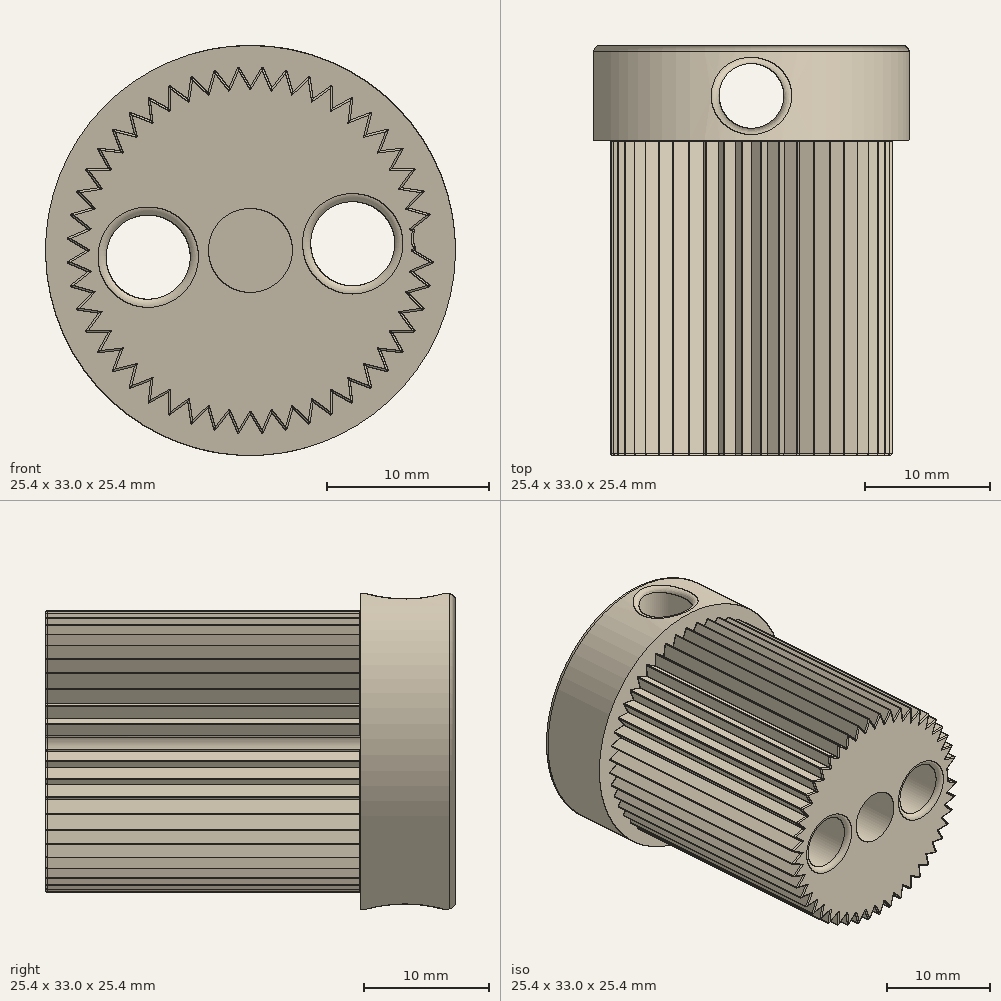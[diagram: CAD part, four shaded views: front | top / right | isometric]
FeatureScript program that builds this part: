
annotation { "Feature Type Name" : "Feature", "Feature Type Description" : "" }
export const myFeature = defineFeature(function(context is Context, id is Id, definition is map)
    precondition{}
    {
        {
            var Q0;
            Q0=qCreatedBy(makeId("Front.planeOp"),FACE);
            var sketch = newSketch(context, id + "F0", { "sketchPlane" : qUnion([Q0])});
            skCircle(sketch, "E0", {"center": v(0, 0) * mm, "radius": 10.16 * mm, "construction": true});
            skCircle(sketch, "E1", {"center": v(0, 0) * mm, "radius": 11.43 * mm, "construction": true});
            skLineSegment(sketch, "E2", {"start": v(0, 0) * mm, "end": v(24.31, 0) * mm, "construction": true});
            skLineSegment(sketch, "E3", {"start": v(0, 0) * mm, "end": v(24.33, -1.6) * mm, "construction": true});
            skLineSegment(sketch, "E4", {"start": v(0, 0) * mm, "end": v(10.07, -1.33) * mm, "construction": true});
            skLineSegment(sketch, "E5", {"start": v(9.53, 0) * mm, "end": v(10.16, 0) * mm});
            skLineSegment(sketch, "E6", {"start": v(10.16, 0) * mm, "end": v(11.4, -0.75) * mm});
            skLineSegment(sketch, "E7", {"start": v(10.07, -1.33) * mm, "end": v(9.44, -1.24) * mm});
            skLineSegment(sketch, "E8", {"start": v(0, 0) * mm, "end": v(9.53, 0) * mm});
            skLineSegment(sketch, "E9", {"start": v(0, 0) * mm, "end": v(9.44, -1.24) * mm});
            skLineSegment(sketch, "E10", {"start": v(11.4, -0.75) * mm, "end": v(10.07, -1.33) * mm});
            skLineSegment(sketch, "E11.trimOffspring", {"start": v(11.33, -1.5) * mm, "end": v(23.43, -3.08) * mm, "construction": true});
            skPoint(sketch, "E12.orphan", {"position": v(10.16, -1.34) * mm});
            skLineSegment(sketch, "E13", {"start": v(17.07, 1.12) * mm, "end": v(-16.43, -1.08) * mm, "construction": true});
            skCircle(sketch, "E14", {"center": v(0, 0) * mm, "radius": 6.35 * mm, "construction": true});
            skCircle(sketch, "E15", {"center": v(-6.34, -0.42) * mm, "radius": 2.6 * mm});
            skCircle(sketch, "E16", {"center": v(6.34, 0.42) * mm, "radius": 2.6 * mm});
            skSolve(sketch);
        }
        {
            var Q0;
            Q0=makeQuery(id+"F0.imprint","IMPRINT",FACE,{"disambiguationData":[TD([[makeQuery(id+"F0.imprint","IMPRINT",EDGE,{"derivedFrom":sQuery(id+"F0.wireOp",EDGE,"E5")}),-1.0]])]});
            var Q1;
            {var subQ0=sQuery(id+"F0.wireOp",EDGE,"E16");var subQ1=sQuery(id+"F0.wireOp",EDGE,"E8");var subQ2=makeQuery(id+"F0.imprint","INTERSECT",VERTEX,{"disambiguationData":[OD(0.0)],"derivedFrom":[subQ1,subQ0]});Q1=makeQuery(id+"F0.imprint","IMPRINT",FACE,{"disambiguationData":[TD([[makeQuery(id+"F0.imprint","IMPRINT",EDGE,{"disambiguationData":[TD([[subQ2,-1.0]])],"derivedFrom":subQ1}),-1.0]])]});}
            var Q2;
            {var subQ0=sQuery(id+"F0.wireOp",EDGE,"E9");var subQ1=sQuery(id+"F0.wireOp",EDGE,"E8");var subQ2=makeQuery(id+"F0.imprint","INTERSECT",VERTEX,{"derivedFrom":[subQ1,subQ0]});Q2=makeQuery(id+"F0.imprint","IMPRINT",FACE,{"disambiguationData":[TD([[makeQuery(id+"F0.imprint","IMPRINT",EDGE,{"disambiguationData":[TD([[subQ2,-1.0]])],"derivedFrom":subQ1}),-1.0]])]});}
            extrude(context, id + "F1", {"entities" : qUnion([Q0, Q1, Q2]), "depth" : 25.4 * mm});
        }
        {
            var Q0;
            Q0=makeQuery(id+"F1.opExtrude","CAP_EDGE",EDGE,{"disambiguationData":[OSD([sQuery(id+"F0.wireOp",EDGE,"E6")])],"isStart":false});
            var Q1;
            Q1=makeQuery(id+"F1.opExtrude","CAP_EDGE",EDGE,{"disambiguationData":[OSD([sQuery(id+"F0.wireOp",EDGE,"E10")])],"isStart":false});
            var Q2;
            Q2=makeQuery(id+"F1.opExtrude","CAP_EDGE",EDGE,{"disambiguationData":[OSD([sQuery(id+"F0.wireOp",EDGE,"E6")])],"isStart":true});
            var Q3;
            Q3=makeQuery(id+"F1.opExtrude","CAP_EDGE",EDGE,{"disambiguationData":[OSD([sQuery(id+"F0.wireOp",EDGE,"E10")])],"isStart":true});
            fillet(context, id + "F2", {"entities" : qUnion([Q0, Q1, Q2, Q3]), "radius" : 0.13 * mm, "tangentPropagation" : true, "allowEdgeOverflow" : false});
        }
        {
            var Q0;
            Q0=makeQuery(id+"F1.opExtrude","SWEPT_EDGE",EDGE,{"disambiguationData":[OSD([sQuery(id+"F0.wireOp",EDGE,"E6"),sQuery(id+"F0.wireOp",EDGE,"E10")])]});
            fillet(context, id + "F3", {"entities" : qUnion([Q0]), "radius" : 0.05 * mm, "tangentPropagation" : true, "allowEdgeOverflow" : false});
        }
        {
            var Q0;
            Q0=makeQuery(id+"F1.opExtrude","SWEPT_BODY",BODY,{"disambiguationData":[OSD([sQuery(id+"F0.wireOp",EDGE,"E5"),sQuery(id+"F0.wireOp",EDGE,"E6"),sQuery(id+"F0.wireOp",EDGE,"gNua0P1m-RBOV-57z6-Uz5b-c0gyhJW3q2aB"),sQuery(id+"F0.wireOp",EDGE,"E7"),sQuery(id+"F0.wireOp",EDGE,"E8"),sQuery(id+"F0.wireOp",EDGE,"E9")])]});
            var Q1;
            Q1=makeQuery(id+"F1.opExtrude","SWEPT_EDGE",EDGE,{"disambiguationData":[OSD([sQuery(id+"F0.wireOp",EDGE,"E8"),sQuery(id+"F0.wireOp",EDGE,"E9")])]});
            circularPattern(context, id + "F4", {"operationType" : NewBodyOperationType.ADD, "entities" : qUnion([Q0]), "axis" : qUnion([Q1]), "angle" : 360 * degree, "instanceCount" : 48, "equalSpace" : true});
        }
        {
            var Q0;
            {var subQ0=makeQuery(id+"F1.opExtrude","CAP_FACE",FACE,{"disambiguationData":[OSD([sQuery(id+"F0.wireOp",EDGE,"E5"),sQuery(id+"F0.wireOp",EDGE,"E6"),sQuery(id+"F0.wireOp",EDGE,"E7"),sQuery(id+"F0.wireOp",EDGE,"E8"),sQuery(id+"F0.wireOp",EDGE,"E9"),sQuery(id+"F0.wireOp",EDGE,"E10")])],"isStart":true});Q0=makeQuery(id+"F4.boolean.opBoolean","MERGE",FACE,{"derivedFrom":[subQ0,makeQuery(id+"F4.opPattern","COPY",FACE,{"derivedFrom":subQ0,"instanceName":"1"}),makeQuery(id+"F4.opPattern","COPY",FACE,{"derivedFrom":subQ0,"instanceName":"2"}),makeQuery(id+"F4.opPattern","COPY",FACE,{"derivedFrom":subQ0,"instanceName":"3"}),makeQuery(id+"F4.opPattern","COPY",FACE,{"derivedFrom":subQ0,"instanceName":"4"}),makeQuery(id+"F4.opPattern","COPY",FACE,{"derivedFrom":subQ0,"instanceName":"5"}),makeQuery(id+"F4.opPattern","COPY",FACE,{"derivedFrom":subQ0,"instanceName":"6"}),makeQuery(id+"F4.opPattern","COPY",FACE,{"derivedFrom":subQ0,"instanceName":"7"}),makeQuery(id+"F4.opPattern","COPY",FACE,{"derivedFrom":subQ0,"instanceName":"8"}),makeQuery(id+"F4.opPattern","COPY",FACE,{"derivedFrom":subQ0,"instanceName":"9"}),makeQuery(id+"F4.opPattern","COPY",FACE,{"derivedFrom":subQ0,"instanceName":"10"}),makeQuery(id+"F4.opPattern","COPY",FACE,{"derivedFrom":subQ0,"instanceName":"11"}),makeQuery(id+"F4.opPattern","COPY",FACE,{"derivedFrom":subQ0,"instanceName":"12"}),makeQuery(id+"F4.opPattern","COPY",FACE,{"derivedFrom":subQ0,"instanceName":"13"}),makeQuery(id+"F4.opPattern","COPY",FACE,{"derivedFrom":subQ0,"instanceName":"14"}),makeQuery(id+"F4.opPattern","COPY",FACE,{"derivedFrom":subQ0,"instanceName":"15"}),makeQuery(id+"F4.opPattern","COPY",FACE,{"derivedFrom":subQ0,"instanceName":"16"}),makeQuery(id+"F4.opPattern","COPY",FACE,{"derivedFrom":subQ0,"instanceName":"17"}),makeQuery(id+"F4.opPattern","COPY",FACE,{"derivedFrom":subQ0,"instanceName":"18"}),makeQuery(id+"F4.opPattern","COPY",FACE,{"derivedFrom":subQ0,"instanceName":"19"}),makeQuery(id+"F4.opPattern","COPY",FACE,{"derivedFrom":subQ0,"instanceName":"20"}),makeQuery(id+"F4.opPattern","COPY",FACE,{"derivedFrom":subQ0,"instanceName":"21"}),makeQuery(id+"F4.opPattern","COPY",FACE,{"derivedFrom":subQ0,"instanceName":"22"}),makeQuery(id+"F4.opPattern","COPY",FACE,{"derivedFrom":subQ0,"instanceName":"23"}),makeQuery(id+"F4.opPattern","COPY",FACE,{"derivedFrom":subQ0,"instanceName":"24"}),makeQuery(id+"F4.opPattern","COPY",FACE,{"derivedFrom":subQ0,"instanceName":"25"}),makeQuery(id+"F4.opPattern","COPY",FACE,{"derivedFrom":subQ0,"instanceName":"26"}),makeQuery(id+"F4.opPattern","COPY",FACE,{"derivedFrom":subQ0,"instanceName":"27"}),makeQuery(id+"F4.opPattern","COPY",FACE,{"derivedFrom":subQ0,"instanceName":"28"}),makeQuery(id+"F4.opPattern","COPY",FACE,{"derivedFrom":subQ0,"instanceName":"29"}),makeQuery(id+"F4.opPattern","COPY",FACE,{"derivedFrom":subQ0,"instanceName":"30"}),makeQuery(id+"F4.opPattern","COPY",FACE,{"derivedFrom":subQ0,"instanceName":"31"}),makeQuery(id+"F4.opPattern","COPY",FACE,{"derivedFrom":subQ0,"instanceName":"32"}),makeQuery(id+"F4.opPattern","COPY",FACE,{"derivedFrom":subQ0,"instanceName":"33"}),makeQuery(id+"F4.opPattern","COPY",FACE,{"derivedFrom":subQ0,"instanceName":"34"}),makeQuery(id+"F4.opPattern","COPY",FACE,{"derivedFrom":subQ0,"instanceName":"35"}),makeQuery(id+"F4.opPattern","COPY",FACE,{"derivedFrom":subQ0,"instanceName":"36"}),makeQuery(id+"F4.opPattern","COPY",FACE,{"derivedFrom":subQ0,"instanceName":"37"}),makeQuery(id+"F4.opPattern","COPY",FACE,{"derivedFrom":subQ0,"instanceName":"38"}),makeQuery(id+"F4.opPattern","COPY",FACE,{"derivedFrom":subQ0,"instanceName":"39"}),makeQuery(id+"F4.opPattern","COPY",FACE,{"derivedFrom":subQ0,"instanceName":"40"}),makeQuery(id+"F4.opPattern","COPY",FACE,{"derivedFrom":subQ0,"instanceName":"41"}),makeQuery(id+"F4.opPattern","COPY",FACE,{"derivedFrom":subQ0,"instanceName":"42"}),makeQuery(id+"F4.opPattern","COPY",FACE,{"derivedFrom":subQ0,"instanceName":"43"}),makeQuery(id+"F4.opPattern","COPY",FACE,{"derivedFrom":subQ0,"instanceName":"44"}),makeQuery(id+"F4.opPattern","COPY",FACE,{"derivedFrom":subQ0,"instanceName":"45"}),makeQuery(id+"F4.opPattern","COPY",FACE,{"derivedFrom":subQ0,"instanceName":"46"}),makeQuery(id+"F4.opPattern","COPY",FACE,{"derivedFrom":subQ0,"instanceName":"47"})]});}
            var sketch = newSketch(context, id + "F5", { "sketchPlane" : qUnion([Q0])});
            skCircle(sketch, "E17", {"center": v(0, 0) * mm, "radius": 12.7 * mm});
            skSolve(sketch);
        }
        {
            var Q0;
            Q0=makeQuery(id+"F5.imprint","IMPRINT",FACE,{"disambiguationData":[TD([[makeQuery(id+"F5.imprint","IMPRINT",EDGE,{"derivedFrom":sQuery(id+"F5.wireOp",EDGE,"E17")}),1.0]])]});
            var Q1;
            {var subQ0=sQuery(id+"F0.wireOp",EDGE,"E10");var subQ1=sQuery(id+"F0.wireOp",EDGE,"E6");var subQ2=makeQuery(id+"F1.opExtrude","CAP_FACE",FACE,{"disambiguationData":[OSD([sQuery(id+"F0.wireOp",EDGE,"E5"),subQ1,sQuery(id+"F0.wireOp",EDGE,"E7"),sQuery(id+"F0.wireOp",EDGE,"E8"),sQuery(id+"F0.wireOp",EDGE,"E9"),subQ0])],"isStart":true});var subQ4=makeQuery(id+"F2.opFillet","BLEND_EDGE",EDGE,{"blendedFrom":[makeQuery(id+"F1.opExtrude","CAP_EDGE",EDGE,{"disambiguationData":[OSD([subQ1])],"isStart":true}),subQ2],"blendedInto":[subQ2]});Q1=makeQuery(id+"F5.imprint","IMPRINT",FACE,{"disambiguationData":[TD([[makeQuery(id+"F5.imprint","IMPRINT",EDGE,{"derivedFrom":subQ4}),1.0]])]});}
            var Q2;
            Q2=sQuery(id+"F5.wireOp",EDGE,"E17");
            extrude(context, id + "F6", {"entities" : qUnion([Q0, Q1]), "operationType" : NewBodyOperationType.ADD, "surfaceEntities" : qUnion([Q2]), "depth" : 7.62 * mm});
        }
        {
            var Q0;
            Q0=makeQuery(id+"F0.imprint","IMPRINT",FACE,{"disambiguationData":[TD([[makeQuery(id+"F0.imprint","IMPRINT",EDGE,{"derivedFrom":sQuery(id+"F0.wireOp",EDGE,"E15")}),1.0]])]});
            var Q1;
            {var subQ0=sQuery(id+"F0.wireOp",EDGE,"E16");var subQ1=sQuery(id+"F0.wireOp",EDGE,"E8");var subQ2=makeQuery(id+"F0.imprint","INTERSECT",VERTEX,{"disambiguationData":[OD(0.0)],"derivedFrom":[subQ1,subQ0]});Q1=makeQuery(id+"F0.imprint","IMPRINT",FACE,{"disambiguationData":[TD([[makeQuery(id+"F0.imprint","IMPRINT",EDGE,{"disambiguationData":[TD([[subQ2,-1.0]])],"derivedFrom":subQ1}),1.0]])]});}
            var Q2;
            {var subQ0=sQuery(id+"F0.wireOp",EDGE,"E16");var subQ1=sQuery(id+"F0.wireOp",EDGE,"E8");var subQ2=makeQuery(id+"F0.imprint","INTERSECT",VERTEX,{"disambiguationData":[OD(0.0)],"derivedFrom":[subQ1,subQ0]});Q2=makeQuery(id+"F0.imprint","IMPRINT",FACE,{"disambiguationData":[TD([[makeQuery(id+"F0.imprint","IMPRINT",EDGE,{"disambiguationData":[TD([[subQ2,-1.0]])],"derivedFrom":subQ1}),-1.0]])]});}
            var Q3;
            {var subQ0=sQuery(id+"F0.wireOp",EDGE,"E16");var subQ1=sQuery(id+"F0.wireOp",EDGE,"E9");var subQ2=makeQuery(id+"F0.imprint","INTERSECT",VERTEX,{"disambiguationData":[OD(0.0)],"derivedFrom":[subQ1,subQ0]});Q3=makeQuery(id+"F0.imprint","IMPRINT",FACE,{"disambiguationData":[TD([[makeQuery(id+"F0.imprint","IMPRINT",EDGE,{"disambiguationData":[TD([[subQ2,-1.0]])],"derivedFrom":subQ1}),-1.0]])]});}
            extrude(context, id + "F7", {"entities" : qUnion([Q0, Q1, Q2, Q3]), "operationType" : NewBodyOperationType.REMOVE, "endBound" : BoundingType.SYMMETRIC, "depth" : 50.8 * mm});
        }
        {
            var Q0;
            {var subQ0=makeQuery(id+"F1.opExtrude","CAP_FACE",FACE,{"disambiguationData":[OSD([sQuery(id+"F0.wireOp",EDGE,"E5"),sQuery(id+"F0.wireOp",EDGE,"E6"),sQuery(id+"F0.wireOp",EDGE,"gNua0P1m-RBOV-57z6-Uz5b-c0gyhJW3q2aB"),sQuery(id+"F0.wireOp",EDGE,"E7"),sQuery(id+"F0.wireOp",EDGE,"E8"),sQuery(id+"F0.wireOp",EDGE,"E9")])],"isStart":false});Q0=makeQuery(id+"F4.boolean.opBoolean","MERGE",FACE,{"derivedFrom":[subQ0,makeQuery(id+"F4.opPattern","COPY",FACE,{"derivedFrom":subQ0,"instanceName":"1"}),makeQuery(id+"F4.opPattern","COPY",FACE,{"derivedFrom":subQ0,"instanceName":"2"}),makeQuery(id+"F4.opPattern","COPY",FACE,{"derivedFrom":subQ0,"instanceName":"3"}),makeQuery(id+"F4.opPattern","COPY",FACE,{"derivedFrom":subQ0,"instanceName":"4"}),makeQuery(id+"F4.opPattern","COPY",FACE,{"derivedFrom":subQ0,"instanceName":"5"}),makeQuery(id+"F4.opPattern","COPY",FACE,{"derivedFrom":subQ0,"instanceName":"6"}),makeQuery(id+"F4.opPattern","COPY",FACE,{"derivedFrom":subQ0,"instanceName":"7"}),makeQuery(id+"F4.opPattern","COPY",FACE,{"derivedFrom":subQ0,"instanceName":"8"}),makeQuery(id+"F4.opPattern","COPY",FACE,{"derivedFrom":subQ0,"instanceName":"9"}),makeQuery(id+"F4.opPattern","COPY",FACE,{"derivedFrom":subQ0,"instanceName":"10"}),makeQuery(id+"F4.opPattern","COPY",FACE,{"derivedFrom":subQ0,"instanceName":"11"}),makeQuery(id+"F4.opPattern","COPY",FACE,{"derivedFrom":subQ0,"instanceName":"12"}),makeQuery(id+"F4.opPattern","COPY",FACE,{"derivedFrom":subQ0,"instanceName":"13"}),makeQuery(id+"F4.opPattern","COPY",FACE,{"derivedFrom":subQ0,"instanceName":"14"}),makeQuery(id+"F4.opPattern","COPY",FACE,{"derivedFrom":subQ0,"instanceName":"15"}),makeQuery(id+"F4.opPattern","COPY",FACE,{"derivedFrom":subQ0,"instanceName":"16"}),makeQuery(id+"F4.opPattern","COPY",FACE,{"derivedFrom":subQ0,"instanceName":"17"}),makeQuery(id+"F4.opPattern","COPY",FACE,{"derivedFrom":subQ0,"instanceName":"18"}),makeQuery(id+"F4.opPattern","COPY",FACE,{"derivedFrom":subQ0,"instanceName":"19"}),makeQuery(id+"F4.opPattern","COPY",FACE,{"derivedFrom":subQ0,"instanceName":"20"}),makeQuery(id+"F4.opPattern","COPY",FACE,{"derivedFrom":subQ0,"instanceName":"21"}),makeQuery(id+"F4.opPattern","COPY",FACE,{"derivedFrom":subQ0,"instanceName":"22"}),makeQuery(id+"F4.opPattern","COPY",FACE,{"derivedFrom":subQ0,"instanceName":"23"}),makeQuery(id+"F4.opPattern","COPY",FACE,{"derivedFrom":subQ0,"instanceName":"24"}),makeQuery(id+"F4.opPattern","COPY",FACE,{"derivedFrom":subQ0,"instanceName":"25"}),makeQuery(id+"F4.opPattern","COPY",FACE,{"derivedFrom":subQ0,"instanceName":"26"}),makeQuery(id+"F4.opPattern","COPY",FACE,{"derivedFrom":subQ0,"instanceName":"27"}),makeQuery(id+"F4.opPattern","COPY",FACE,{"derivedFrom":subQ0,"instanceName":"28"}),makeQuery(id+"F4.opPattern","COPY",FACE,{"derivedFrom":subQ0,"instanceName":"29"}),makeQuery(id+"F4.opPattern","COPY",FACE,{"derivedFrom":subQ0,"instanceName":"30"}),makeQuery(id+"F4.opPattern","COPY",FACE,{"derivedFrom":subQ0,"instanceName":"31"}),makeQuery(id+"F4.opPattern","COPY",FACE,{"derivedFrom":subQ0,"instanceName":"32"}),makeQuery(id+"F4.opPattern","COPY",FACE,{"derivedFrom":subQ0,"instanceName":"33"}),makeQuery(id+"F4.opPattern","COPY",FACE,{"derivedFrom":subQ0,"instanceName":"34"}),makeQuery(id+"F4.opPattern","COPY",FACE,{"derivedFrom":subQ0,"instanceName":"35"}),makeQuery(id+"F4.opPattern","COPY",FACE,{"derivedFrom":subQ0,"instanceName":"36"}),makeQuery(id+"F4.opPattern","COPY",FACE,{"derivedFrom":subQ0,"instanceName":"37"}),makeQuery(id+"F4.opPattern","COPY",FACE,{"derivedFrom":subQ0,"instanceName":"38"}),makeQuery(id+"F4.opPattern","COPY",FACE,{"derivedFrom":subQ0,"instanceName":"39"}),makeQuery(id+"F4.opPattern","COPY",FACE,{"derivedFrom":subQ0,"instanceName":"40"}),makeQuery(id+"F4.opPattern","COPY",FACE,{"derivedFrom":subQ0,"instanceName":"41"}),makeQuery(id+"F4.opPattern","COPY",FACE,{"derivedFrom":subQ0,"instanceName":"42"}),makeQuery(id+"F4.opPattern","COPY",FACE,{"derivedFrom":subQ0,"instanceName":"43"}),makeQuery(id+"F4.opPattern","COPY",FACE,{"derivedFrom":subQ0,"instanceName":"44"}),makeQuery(id+"F4.opPattern","COPY",FACE,{"derivedFrom":subQ0,"instanceName":"45"}),makeQuery(id+"F4.opPattern","COPY",FACE,{"derivedFrom":subQ0,"instanceName":"46"}),makeQuery(id+"F4.opPattern","COPY",FACE,{"derivedFrom":subQ0,"instanceName":"47"}),makeQuery(id+"F4.opPattern","COPY",FACE,{"derivedFrom":subQ0,"instanceName":"48"}),makeQuery(id+"F4.opPattern","COPY",FACE,{"derivedFrom":subQ0,"instanceName":"49"}),makeQuery(id+"F4.opPattern","COPY",FACE,{"derivedFrom":subQ0,"instanceName":"50"}),makeQuery(id+"F4.opPattern","COPY",FACE,{"derivedFrom":subQ0,"instanceName":"51"}),makeQuery(id+"F4.opPattern","COPY",FACE,{"derivedFrom":subQ0,"instanceName":"52"}),makeQuery(id+"F4.opPattern","COPY",FACE,{"derivedFrom":subQ0,"instanceName":"53"}),makeQuery(id+"F4.opPattern","COPY",FACE,{"derivedFrom":subQ0,"instanceName":"54"}),makeQuery(id+"F4.opPattern","COPY",FACE,{"derivedFrom":subQ0,"instanceName":"55"}),makeQuery(id+"F4.opPattern","COPY",FACE,{"derivedFrom":subQ0,"instanceName":"56"}),makeQuery(id+"F4.opPattern","COPY",FACE,{"derivedFrom":subQ0,"instanceName":"57"}),makeQuery(id+"F4.opPattern","COPY",FACE,{"derivedFrom":subQ0,"instanceName":"58"}),makeQuery(id+"F4.opPattern","COPY",FACE,{"derivedFrom":subQ0,"instanceName":"59"}),makeQuery(id+"F4.opPattern","COPY",FACE,{"derivedFrom":subQ0,"instanceName":"60"}),makeQuery(id+"F4.opPattern","COPY",FACE,{"derivedFrom":subQ0,"instanceName":"61"}),makeQuery(id+"F4.opPattern","COPY",FACE,{"derivedFrom":subQ0,"instanceName":"62"}),makeQuery(id+"F4.opPattern","COPY",FACE,{"derivedFrom":subQ0,"instanceName":"63"}),makeQuery(id+"F4.opPattern","COPY",FACE,{"derivedFrom":subQ0,"instanceName":"64"}),makeQuery(id+"F4.opPattern","COPY",FACE,{"derivedFrom":subQ0,"instanceName":"65"}),makeQuery(id+"F4.opPattern","COPY",FACE,{"derivedFrom":subQ0,"instanceName":"66"}),makeQuery(id+"F4.opPattern","COPY",FACE,{"derivedFrom":subQ0,"instanceName":"67"}),makeQuery(id+"F4.opPattern","COPY",FACE,{"derivedFrom":subQ0,"instanceName":"68"}),makeQuery(id+"F4.opPattern","COPY",FACE,{"derivedFrom":subQ0,"instanceName":"69"}),makeQuery(id+"F4.opPattern","COPY",FACE,{"derivedFrom":subQ0,"instanceName":"70"}),makeQuery(id+"F4.opPattern","COPY",FACE,{"derivedFrom":subQ0,"instanceName":"71"})]});}
            var sketch = newSketch(context, id + "F8", { "sketchPlane" : qUnion([Q0])});
            skCircle(sketch, "E18", {"center": v(0, 0) * mm, "radius": 9.59 * mm});
            skLineSegment(sketch, "E19", {"start": v(0, 0) * mm, "end": v(11.91, 0) * mm, "construction": true});
            skLineSegment(sketch, "E20", {"start": v(0, 0) * mm, "end": v(12.83, 0.84) * mm, "construction": true});
            skCircle(sketch, "E21", {"center": v(10.07, 0.66) * mm, "radius": 0.5 * mm});
            skCircle(sketch, "E22", {"center": v(0, 0) * mm, "radius": 2.6 * mm});
            skSolve(sketch);
        }
        {
            var Q0;
            {var subQ0=makeQuery(id+"F1.opExtrude","CAP_FACE",FACE,{"disambiguationData":[OSD([sQuery(id+"F0.wireOp",EDGE,"E5"),sQuery(id+"F0.wireOp",EDGE,"E6"),sQuery(id+"F0.wireOp",EDGE,"E7"),sQuery(id+"F0.wireOp",EDGE,"E8"),sQuery(id+"F0.wireOp",EDGE,"E9"),sQuery(id+"F0.wireOp",EDGE,"E10")])],"isStart":false});Q0=makeQuery(id+"F4.boolean.opBoolean","MERGE",FACE,{"derivedFrom":[subQ0,makeQuery(id+"F4.opPattern","COPY",FACE,{"derivedFrom":subQ0,"instanceName":"1"}),makeQuery(id+"F4.opPattern","COPY",FACE,{"derivedFrom":subQ0,"instanceName":"2"}),makeQuery(id+"F4.opPattern","COPY",FACE,{"derivedFrom":subQ0,"instanceName":"3"}),makeQuery(id+"F4.opPattern","COPY",FACE,{"derivedFrom":subQ0,"instanceName":"4"}),makeQuery(id+"F4.opPattern","COPY",FACE,{"derivedFrom":subQ0,"instanceName":"5"}),makeQuery(id+"F4.opPattern","COPY",FACE,{"derivedFrom":subQ0,"instanceName":"6"}),makeQuery(id+"F4.opPattern","COPY",FACE,{"derivedFrom":subQ0,"instanceName":"7"}),makeQuery(id+"F4.opPattern","COPY",FACE,{"derivedFrom":subQ0,"instanceName":"8"}),makeQuery(id+"F4.opPattern","COPY",FACE,{"derivedFrom":subQ0,"instanceName":"9"}),makeQuery(id+"F4.opPattern","COPY",FACE,{"derivedFrom":subQ0,"instanceName":"10"}),makeQuery(id+"F4.opPattern","COPY",FACE,{"derivedFrom":subQ0,"instanceName":"11"}),makeQuery(id+"F4.opPattern","COPY",FACE,{"derivedFrom":subQ0,"instanceName":"12"}),makeQuery(id+"F4.opPattern","COPY",FACE,{"derivedFrom":subQ0,"instanceName":"13"}),makeQuery(id+"F4.opPattern","COPY",FACE,{"derivedFrom":subQ0,"instanceName":"14"}),makeQuery(id+"F4.opPattern","COPY",FACE,{"derivedFrom":subQ0,"instanceName":"15"}),makeQuery(id+"F4.opPattern","COPY",FACE,{"derivedFrom":subQ0,"instanceName":"16"}),makeQuery(id+"F4.opPattern","COPY",FACE,{"derivedFrom":subQ0,"instanceName":"17"}),makeQuery(id+"F4.opPattern","COPY",FACE,{"derivedFrom":subQ0,"instanceName":"18"}),makeQuery(id+"F4.opPattern","COPY",FACE,{"derivedFrom":subQ0,"instanceName":"19"}),makeQuery(id+"F4.opPattern","COPY",FACE,{"derivedFrom":subQ0,"instanceName":"20"}),makeQuery(id+"F4.opPattern","COPY",FACE,{"derivedFrom":subQ0,"instanceName":"21"}),makeQuery(id+"F4.opPattern","COPY",FACE,{"derivedFrom":subQ0,"instanceName":"22"}),makeQuery(id+"F4.opPattern","COPY",FACE,{"derivedFrom":subQ0,"instanceName":"23"}),makeQuery(id+"F4.opPattern","COPY",FACE,{"derivedFrom":subQ0,"instanceName":"24"}),makeQuery(id+"F4.opPattern","COPY",FACE,{"derivedFrom":subQ0,"instanceName":"25"}),makeQuery(id+"F4.opPattern","COPY",FACE,{"derivedFrom":subQ0,"instanceName":"26"}),makeQuery(id+"F4.opPattern","COPY",FACE,{"derivedFrom":subQ0,"instanceName":"27"}),makeQuery(id+"F4.opPattern","COPY",FACE,{"derivedFrom":subQ0,"instanceName":"28"}),makeQuery(id+"F4.opPattern","COPY",FACE,{"derivedFrom":subQ0,"instanceName":"29"}),makeQuery(id+"F4.opPattern","COPY",FACE,{"derivedFrom":subQ0,"instanceName":"30"}),makeQuery(id+"F4.opPattern","COPY",FACE,{"derivedFrom":subQ0,"instanceName":"31"}),makeQuery(id+"F4.opPattern","COPY",FACE,{"derivedFrom":subQ0,"instanceName":"32"}),makeQuery(id+"F4.opPattern","COPY",FACE,{"derivedFrom":subQ0,"instanceName":"33"}),makeQuery(id+"F4.opPattern","COPY",FACE,{"derivedFrom":subQ0,"instanceName":"34"}),makeQuery(id+"F4.opPattern","COPY",FACE,{"derivedFrom":subQ0,"instanceName":"35"}),makeQuery(id+"F4.opPattern","COPY",FACE,{"derivedFrom":subQ0,"instanceName":"36"}),makeQuery(id+"F4.opPattern","COPY",FACE,{"derivedFrom":subQ0,"instanceName":"37"}),makeQuery(id+"F4.opPattern","COPY",FACE,{"derivedFrom":subQ0,"instanceName":"38"}),makeQuery(id+"F4.opPattern","COPY",FACE,{"derivedFrom":subQ0,"instanceName":"39"}),makeQuery(id+"F4.opPattern","COPY",FACE,{"derivedFrom":subQ0,"instanceName":"40"}),makeQuery(id+"F4.opPattern","COPY",FACE,{"derivedFrom":subQ0,"instanceName":"41"}),makeQuery(id+"F4.opPattern","COPY",FACE,{"derivedFrom":subQ0,"instanceName":"42"}),makeQuery(id+"F4.opPattern","COPY",FACE,{"derivedFrom":subQ0,"instanceName":"43"}),makeQuery(id+"F4.opPattern","COPY",FACE,{"derivedFrom":subQ0,"instanceName":"44"}),makeQuery(id+"F4.opPattern","COPY",FACE,{"derivedFrom":subQ0,"instanceName":"45"}),makeQuery(id+"F4.opPattern","COPY",FACE,{"derivedFrom":subQ0,"instanceName":"46"}),makeQuery(id+"F4.opPattern","COPY",FACE,{"derivedFrom":subQ0,"instanceName":"47"})]});}
            var sketch = newSketch(context, id + "F9", { "sketchPlane" : qUnion([Q0])});
            skCircle(sketch, "E23", {"center": v(11.13, 0.73) * mm, "radius": 1.05 * mm});
            skSolve(sketch);
        }
        {
            var Q0;
            Q0 = qSketchRegion(id + "F9", true);
            var Q1;
            Q1=makeQuery(id+"F6.opExtrude","CAP_FACE",FACE,{"disambiguationData":[OSD([sQuery(id+"F5.wireOp",EDGE,"E17")])],"isStart":true});
            extrude(context, id + "F10", {"entities" : qUnion([Q0]), "operationType" : NewBodyOperationType.REMOVE, "endBound" : BoundingType.UP_TO_SURFACE, "oppositeDirection" : true, "endBoundEntityFace" : qUnion([Q1]), "depth" : 25.4 * mm});
        }
        {
            var Q0;
            Q0=makeQuery(id+"F8.imprint","IMPRINT",FACE,{"disambiguationData":[TD([[makeQuery(id+"F8.imprint","IMPRINT",EDGE,{"derivedFrom":sQuery(id+"F8.wireOp",EDGE,"E22")}),1.0]])]});
            var Q1;
            Q1=sQuery(id+"F8.wireOp",EDGE,"E22");
            extrude(context, id + "F11", {"entities" : qUnion([Q0]), "operationType" : NewBodyOperationType.REMOVE, "surfaceEntities" : qUnion([Q1]), "oppositeDirection" : true, "depth" : 22.86 * mm});
        }
        {
            var Q0;
            Q0=makeQuery(id+"F10.boolean.opBoolean","INTERSECT",EDGE,{"derivedFrom":[makeQuery(id+"F4.opPattern","COPY",FACE,{"derivedFrom":makeQuery(id+"F1.opExtrude","SWEPT_FACE",FACE,{"disambiguationData":[OSD([sQuery(id+"F0.wireOp",EDGE,"E6")])]}),"instanceName":"47"}),makeQuery(id+"F10.opExtrude","SWEPT_FACE",FACE,{"disambiguationData":[OSD([sQuery(id+"F9.wireOp",EDGE,"E23")])]})]});
            var Q1;
            Q1=makeQuery(id+"F10.boolean.opBoolean","COPY",EDGE,{"derivedFrom":makeQuery(id+"F10.opExtrude","CAP_EDGE",EDGE,{"disambiguationData":[OSD([sQuery(id+"F9.wireOp",EDGE,"E23")])],"isStart":true})});
            fillet(context, id + "F12", {"entities" : qUnion([Q0, Q1]), "radius" : 0.13 * mm, "tangentPropagation" : true, "allowEdgeOverflow" : false});
        }
        {
            var Q0;
            Q0=qCreatedBy(makeId("Top.planeOp"),FACE);
            var sketch = newSketch(context, id + "F13", { "sketchPlane" : qUnion([Q0])});
            skLineSegment(sketch, "E24", {"start": v(-12.7, 0) * mm, "end": v(-12.7, 7.62) * mm});
            skLineSegment(sketch, "E25", {"start": v(12.7, 7.62) * mm, "end": v(12.7, 0) * mm});
            skCircle(sketch, "E26", {"center": v(0, 3.56) * mm, "radius": 2.6 * mm});
            skSolve(sketch);
        }
        {
            var Q0;
            Q0 = qSketchRegion(id + "F13", true);
            var Q1;
            Q1=sQuery(id+"F13.wireOp",EDGE,"E26");
            extrude(context, id + "F14", {"entities" : qUnion([Q0]), "operationType" : NewBodyOperationType.REMOVE, "surfaceEntities" : qUnion([Q1]), "endBound" : BoundingType.SYMMETRIC, "oppositeDirection" : true, "depth" : 25.4 * mm});
        }
        {
            var Q0;
            Q0=makeQuery(id+"F7.boolean.opBoolean","COPY",EDGE,{"derivedFrom":makeQuery(id+"F7.opExtrude","CAP_EDGE",EDGE,{"disambiguationData":[OSD([sQuery(id+"F0.wireOp",EDGE,"E16")])],"isStart":true})});
            var Q1;
            Q1=makeQuery(id+"F7.boolean.opBoolean","COPY",EDGE,{"derivedFrom":makeQuery(id+"F7.opExtrude","CAP_EDGE",EDGE,{"disambiguationData":[OSD([sQuery(id+"F0.wireOp",EDGE,"E15")])],"isStart":true})});
            var Q2;
            {var subQ0=makeQuery(id+"F1.opExtrude","CAP_FACE",FACE,{"disambiguationData":[OSD([sQuery(id+"F0.wireOp",EDGE,"E5"),sQuery(id+"F0.wireOp",EDGE,"E6"),sQuery(id+"F0.wireOp",EDGE,"E7"),sQuery(id+"F0.wireOp",EDGE,"E8"),sQuery(id+"F0.wireOp",EDGE,"E9"),sQuery(id+"F0.wireOp",EDGE,"E10")])],"isStart":false});Q2=makeQuery(id+"F7.boolean.opBoolean","INTERSECT",EDGE,{"derivedFrom":[makeQuery(id+"F4.boolean.opBoolean","MERGE",FACE,{"derivedFrom":[subQ0,makeQuery(id+"F4.opPattern","COPY",FACE,{"derivedFrom":subQ0,"instanceName":"1"}),makeQuery(id+"F4.opPattern","COPY",FACE,{"derivedFrom":subQ0,"instanceName":"2"}),makeQuery(id+"F4.opPattern","COPY",FACE,{"derivedFrom":subQ0,"instanceName":"3"}),makeQuery(id+"F4.opPattern","COPY",FACE,{"derivedFrom":subQ0,"instanceName":"4"}),makeQuery(id+"F4.opPattern","COPY",FACE,{"derivedFrom":subQ0,"instanceName":"5"}),makeQuery(id+"F4.opPattern","COPY",FACE,{"derivedFrom":subQ0,"instanceName":"6"}),makeQuery(id+"F4.opPattern","COPY",FACE,{"derivedFrom":subQ0,"instanceName":"7"}),makeQuery(id+"F4.opPattern","COPY",FACE,{"derivedFrom":subQ0,"instanceName":"8"}),makeQuery(id+"F4.opPattern","COPY",FACE,{"derivedFrom":subQ0,"instanceName":"9"}),makeQuery(id+"F4.opPattern","COPY",FACE,{"derivedFrom":subQ0,"instanceName":"10"}),makeQuery(id+"F4.opPattern","COPY",FACE,{"derivedFrom":subQ0,"instanceName":"11"}),makeQuery(id+"F4.opPattern","COPY",FACE,{"derivedFrom":subQ0,"instanceName":"12"}),makeQuery(id+"F4.opPattern","COPY",FACE,{"derivedFrom":subQ0,"instanceName":"13"}),makeQuery(id+"F4.opPattern","COPY",FACE,{"derivedFrom":subQ0,"instanceName":"14"}),makeQuery(id+"F4.opPattern","COPY",FACE,{"derivedFrom":subQ0,"instanceName":"15"}),makeQuery(id+"F4.opPattern","COPY",FACE,{"derivedFrom":subQ0,"instanceName":"16"}),makeQuery(id+"F4.opPattern","COPY",FACE,{"derivedFrom":subQ0,"instanceName":"17"}),makeQuery(id+"F4.opPattern","COPY",FACE,{"derivedFrom":subQ0,"instanceName":"18"}),makeQuery(id+"F4.opPattern","COPY",FACE,{"derivedFrom":subQ0,"instanceName":"19"}),makeQuery(id+"F4.opPattern","COPY",FACE,{"derivedFrom":subQ0,"instanceName":"20"}),makeQuery(id+"F4.opPattern","COPY",FACE,{"derivedFrom":subQ0,"instanceName":"21"}),makeQuery(id+"F4.opPattern","COPY",FACE,{"derivedFrom":subQ0,"instanceName":"22"}),makeQuery(id+"F4.opPattern","COPY",FACE,{"derivedFrom":subQ0,"instanceName":"23"}),makeQuery(id+"F4.opPattern","COPY",FACE,{"derivedFrom":subQ0,"instanceName":"24"}),makeQuery(id+"F4.opPattern","COPY",FACE,{"derivedFrom":subQ0,"instanceName":"25"}),makeQuery(id+"F4.opPattern","COPY",FACE,{"derivedFrom":subQ0,"instanceName":"26"}),makeQuery(id+"F4.opPattern","COPY",FACE,{"derivedFrom":subQ0,"instanceName":"27"}),makeQuery(id+"F4.opPattern","COPY",FACE,{"derivedFrom":subQ0,"instanceName":"28"}),makeQuery(id+"F4.opPattern","COPY",FACE,{"derivedFrom":subQ0,"instanceName":"29"}),makeQuery(id+"F4.opPattern","COPY",FACE,{"derivedFrom":subQ0,"instanceName":"30"}),makeQuery(id+"F4.opPattern","COPY",FACE,{"derivedFrom":subQ0,"instanceName":"31"}),makeQuery(id+"F4.opPattern","COPY",FACE,{"derivedFrom":subQ0,"instanceName":"32"}),makeQuery(id+"F4.opPattern","COPY",FACE,{"derivedFrom":subQ0,"instanceName":"33"}),makeQuery(id+"F4.opPattern","COPY",FACE,{"derivedFrom":subQ0,"instanceName":"34"}),makeQuery(id+"F4.opPattern","COPY",FACE,{"derivedFrom":subQ0,"instanceName":"35"}),makeQuery(id+"F4.opPattern","COPY",FACE,{"derivedFrom":subQ0,"instanceName":"36"}),makeQuery(id+"F4.opPattern","COPY",FACE,{"derivedFrom":subQ0,"instanceName":"37"}),makeQuery(id+"F4.opPattern","COPY",FACE,{"derivedFrom":subQ0,"instanceName":"38"}),makeQuery(id+"F4.opPattern","COPY",FACE,{"derivedFrom":subQ0,"instanceName":"39"}),makeQuery(id+"F4.opPattern","COPY",FACE,{"derivedFrom":subQ0,"instanceName":"40"}),makeQuery(id+"F4.opPattern","COPY",FACE,{"derivedFrom":subQ0,"instanceName":"41"}),makeQuery(id+"F4.opPattern","COPY",FACE,{"derivedFrom":subQ0,"instanceName":"42"}),makeQuery(id+"F4.opPattern","COPY",FACE,{"derivedFrom":subQ0,"instanceName":"43"}),makeQuery(id+"F4.opPattern","COPY",FACE,{"derivedFrom":subQ0,"instanceName":"44"}),makeQuery(id+"F4.opPattern","COPY",FACE,{"derivedFrom":subQ0,"instanceName":"45"}),makeQuery(id+"F4.opPattern","COPY",FACE,{"derivedFrom":subQ0,"instanceName":"46"}),makeQuery(id+"F4.opPattern","COPY",FACE,{"derivedFrom":subQ0,"instanceName":"47"})]}),makeQuery(id+"F7.opExtrude","SWEPT_FACE",FACE,{"disambiguationData":[OSD([sQuery(id+"F0.wireOp",EDGE,"E15")])]})]});}
            var Q3;
            {var subQ0=makeQuery(id+"F1.opExtrude","CAP_FACE",FACE,{"disambiguationData":[OSD([sQuery(id+"F0.wireOp",EDGE,"E5"),sQuery(id+"F0.wireOp",EDGE,"E6"),sQuery(id+"F0.wireOp",EDGE,"E7"),sQuery(id+"F0.wireOp",EDGE,"E8"),sQuery(id+"F0.wireOp",EDGE,"E9"),sQuery(id+"F0.wireOp",EDGE,"E10")])],"isStart":false});Q3=makeQuery(id+"F7.boolean.opBoolean","INTERSECT",EDGE,{"derivedFrom":[makeQuery(id+"F4.boolean.opBoolean","MERGE",FACE,{"derivedFrom":[subQ0,makeQuery(id+"F4.opPattern","COPY",FACE,{"derivedFrom":subQ0,"instanceName":"1"}),makeQuery(id+"F4.opPattern","COPY",FACE,{"derivedFrom":subQ0,"instanceName":"2"}),makeQuery(id+"F4.opPattern","COPY",FACE,{"derivedFrom":subQ0,"instanceName":"3"}),makeQuery(id+"F4.opPattern","COPY",FACE,{"derivedFrom":subQ0,"instanceName":"4"}),makeQuery(id+"F4.opPattern","COPY",FACE,{"derivedFrom":subQ0,"instanceName":"5"}),makeQuery(id+"F4.opPattern","COPY",FACE,{"derivedFrom":subQ0,"instanceName":"6"}),makeQuery(id+"F4.opPattern","COPY",FACE,{"derivedFrom":subQ0,"instanceName":"7"}),makeQuery(id+"F4.opPattern","COPY",FACE,{"derivedFrom":subQ0,"instanceName":"8"}),makeQuery(id+"F4.opPattern","COPY",FACE,{"derivedFrom":subQ0,"instanceName":"9"}),makeQuery(id+"F4.opPattern","COPY",FACE,{"derivedFrom":subQ0,"instanceName":"10"}),makeQuery(id+"F4.opPattern","COPY",FACE,{"derivedFrom":subQ0,"instanceName":"11"}),makeQuery(id+"F4.opPattern","COPY",FACE,{"derivedFrom":subQ0,"instanceName":"12"}),makeQuery(id+"F4.opPattern","COPY",FACE,{"derivedFrom":subQ0,"instanceName":"13"}),makeQuery(id+"F4.opPattern","COPY",FACE,{"derivedFrom":subQ0,"instanceName":"14"}),makeQuery(id+"F4.opPattern","COPY",FACE,{"derivedFrom":subQ0,"instanceName":"15"}),makeQuery(id+"F4.opPattern","COPY",FACE,{"derivedFrom":subQ0,"instanceName":"16"}),makeQuery(id+"F4.opPattern","COPY",FACE,{"derivedFrom":subQ0,"instanceName":"17"}),makeQuery(id+"F4.opPattern","COPY",FACE,{"derivedFrom":subQ0,"instanceName":"18"}),makeQuery(id+"F4.opPattern","COPY",FACE,{"derivedFrom":subQ0,"instanceName":"19"}),makeQuery(id+"F4.opPattern","COPY",FACE,{"derivedFrom":subQ0,"instanceName":"20"}),makeQuery(id+"F4.opPattern","COPY",FACE,{"derivedFrom":subQ0,"instanceName":"21"}),makeQuery(id+"F4.opPattern","COPY",FACE,{"derivedFrom":subQ0,"instanceName":"22"}),makeQuery(id+"F4.opPattern","COPY",FACE,{"derivedFrom":subQ0,"instanceName":"23"}),makeQuery(id+"F4.opPattern","COPY",FACE,{"derivedFrom":subQ0,"instanceName":"24"}),makeQuery(id+"F4.opPattern","COPY",FACE,{"derivedFrom":subQ0,"instanceName":"25"}),makeQuery(id+"F4.opPattern","COPY",FACE,{"derivedFrom":subQ0,"instanceName":"26"}),makeQuery(id+"F4.opPattern","COPY",FACE,{"derivedFrom":subQ0,"instanceName":"27"}),makeQuery(id+"F4.opPattern","COPY",FACE,{"derivedFrom":subQ0,"instanceName":"28"}),makeQuery(id+"F4.opPattern","COPY",FACE,{"derivedFrom":subQ0,"instanceName":"29"}),makeQuery(id+"F4.opPattern","COPY",FACE,{"derivedFrom":subQ0,"instanceName":"30"}),makeQuery(id+"F4.opPattern","COPY",FACE,{"derivedFrom":subQ0,"instanceName":"31"}),makeQuery(id+"F4.opPattern","COPY",FACE,{"derivedFrom":subQ0,"instanceName":"32"}),makeQuery(id+"F4.opPattern","COPY",FACE,{"derivedFrom":subQ0,"instanceName":"33"}),makeQuery(id+"F4.opPattern","COPY",FACE,{"derivedFrom":subQ0,"instanceName":"34"}),makeQuery(id+"F4.opPattern","COPY",FACE,{"derivedFrom":subQ0,"instanceName":"35"}),makeQuery(id+"F4.opPattern","COPY",FACE,{"derivedFrom":subQ0,"instanceName":"36"}),makeQuery(id+"F4.opPattern","COPY",FACE,{"derivedFrom":subQ0,"instanceName":"37"}),makeQuery(id+"F4.opPattern","COPY",FACE,{"derivedFrom":subQ0,"instanceName":"38"}),makeQuery(id+"F4.opPattern","COPY",FACE,{"derivedFrom":subQ0,"instanceName":"39"}),makeQuery(id+"F4.opPattern","COPY",FACE,{"derivedFrom":subQ0,"instanceName":"40"}),makeQuery(id+"F4.opPattern","COPY",FACE,{"derivedFrom":subQ0,"instanceName":"41"}),makeQuery(id+"F4.opPattern","COPY",FACE,{"derivedFrom":subQ0,"instanceName":"42"}),makeQuery(id+"F4.opPattern","COPY",FACE,{"derivedFrom":subQ0,"instanceName":"43"}),makeQuery(id+"F4.opPattern","COPY",FACE,{"derivedFrom":subQ0,"instanceName":"44"}),makeQuery(id+"F4.opPattern","COPY",FACE,{"derivedFrom":subQ0,"instanceName":"45"}),makeQuery(id+"F4.opPattern","COPY",FACE,{"derivedFrom":subQ0,"instanceName":"46"}),makeQuery(id+"F4.opPattern","COPY",FACE,{"derivedFrom":subQ0,"instanceName":"47"})]}),makeQuery(id+"F7.opExtrude","SWEPT_FACE",FACE,{"disambiguationData":[OSD([sQuery(id+"F0.wireOp",EDGE,"E16")])]})]});}
            var Q4;
            Q4=makeQuery(id+"F11.boolean.opBoolean","COPY",EDGE,{"derivedFrom":makeQuery(id+"F11.opExtrude","CAP_EDGE",EDGE,{"disambiguationData":[OSD([sQuery(id+"F8.wireOp",EDGE,"E22")])],"isStart":true})});
            var Q5;
            {var subQ0=makeQuery(id+"F1.opExtrude","CAP_FACE",FACE,{"disambiguationData":[OSD([sQuery(id+"F0.wireOp",EDGE,"E5"),sQuery(id+"F0.wireOp",EDGE,"E6"),sQuery(id+"F0.wireOp",EDGE,"E7"),sQuery(id+"F0.wireOp",EDGE,"E8"),sQuery(id+"F0.wireOp",EDGE,"E9"),sQuery(id+"F0.wireOp",EDGE,"E10")])],"isStart":true});Q5=makeQuery(id+"F11.boolean.opBoolean","INTERSECT",EDGE,{"derivedFrom":[makeQuery(id+"F4.boolean.opBoolean","MERGE",FACE,{"derivedFrom":[subQ0,makeQuery(id+"F4.opPattern","COPY",FACE,{"derivedFrom":subQ0,"instanceName":"1"}),makeQuery(id+"F4.opPattern","COPY",FACE,{"derivedFrom":subQ0,"instanceName":"2"}),makeQuery(id+"F4.opPattern","COPY",FACE,{"derivedFrom":subQ0,"instanceName":"3"}),makeQuery(id+"F4.opPattern","COPY",FACE,{"derivedFrom":subQ0,"instanceName":"4"}),makeQuery(id+"F4.opPattern","COPY",FACE,{"derivedFrom":subQ0,"instanceName":"5"}),makeQuery(id+"F4.opPattern","COPY",FACE,{"derivedFrom":subQ0,"instanceName":"6"}),makeQuery(id+"F4.opPattern","COPY",FACE,{"derivedFrom":subQ0,"instanceName":"7"}),makeQuery(id+"F4.opPattern","COPY",FACE,{"derivedFrom":subQ0,"instanceName":"8"}),makeQuery(id+"F4.opPattern","COPY",FACE,{"derivedFrom":subQ0,"instanceName":"9"}),makeQuery(id+"F4.opPattern","COPY",FACE,{"derivedFrom":subQ0,"instanceName":"10"}),makeQuery(id+"F4.opPattern","COPY",FACE,{"derivedFrom":subQ0,"instanceName":"11"}),makeQuery(id+"F4.opPattern","COPY",FACE,{"derivedFrom":subQ0,"instanceName":"12"}),makeQuery(id+"F4.opPattern","COPY",FACE,{"derivedFrom":subQ0,"instanceName":"13"}),makeQuery(id+"F4.opPattern","COPY",FACE,{"derivedFrom":subQ0,"instanceName":"14"}),makeQuery(id+"F4.opPattern","COPY",FACE,{"derivedFrom":subQ0,"instanceName":"15"}),makeQuery(id+"F4.opPattern","COPY",FACE,{"derivedFrom":subQ0,"instanceName":"16"}),makeQuery(id+"F4.opPattern","COPY",FACE,{"derivedFrom":subQ0,"instanceName":"17"}),makeQuery(id+"F4.opPattern","COPY",FACE,{"derivedFrom":subQ0,"instanceName":"18"}),makeQuery(id+"F4.opPattern","COPY",FACE,{"derivedFrom":subQ0,"instanceName":"19"}),makeQuery(id+"F4.opPattern","COPY",FACE,{"derivedFrom":subQ0,"instanceName":"20"}),makeQuery(id+"F4.opPattern","COPY",FACE,{"derivedFrom":subQ0,"instanceName":"21"}),makeQuery(id+"F4.opPattern","COPY",FACE,{"derivedFrom":subQ0,"instanceName":"22"}),makeQuery(id+"F4.opPattern","COPY",FACE,{"derivedFrom":subQ0,"instanceName":"23"}),makeQuery(id+"F4.opPattern","COPY",FACE,{"derivedFrom":subQ0,"instanceName":"24"}),makeQuery(id+"F4.opPattern","COPY",FACE,{"derivedFrom":subQ0,"instanceName":"25"}),makeQuery(id+"F4.opPattern","COPY",FACE,{"derivedFrom":subQ0,"instanceName":"26"}),makeQuery(id+"F4.opPattern","COPY",FACE,{"derivedFrom":subQ0,"instanceName":"27"}),makeQuery(id+"F4.opPattern","COPY",FACE,{"derivedFrom":subQ0,"instanceName":"28"}),makeQuery(id+"F4.opPattern","COPY",FACE,{"derivedFrom":subQ0,"instanceName":"29"}),makeQuery(id+"F4.opPattern","COPY",FACE,{"derivedFrom":subQ0,"instanceName":"30"}),makeQuery(id+"F4.opPattern","COPY",FACE,{"derivedFrom":subQ0,"instanceName":"31"}),makeQuery(id+"F4.opPattern","COPY",FACE,{"derivedFrom":subQ0,"instanceName":"32"}),makeQuery(id+"F4.opPattern","COPY",FACE,{"derivedFrom":subQ0,"instanceName":"33"}),makeQuery(id+"F4.opPattern","COPY",FACE,{"derivedFrom":subQ0,"instanceName":"34"}),makeQuery(id+"F4.opPattern","COPY",FACE,{"derivedFrom":subQ0,"instanceName":"35"}),makeQuery(id+"F4.opPattern","COPY",FACE,{"derivedFrom":subQ0,"instanceName":"36"}),makeQuery(id+"F4.opPattern","COPY",FACE,{"derivedFrom":subQ0,"instanceName":"37"}),makeQuery(id+"F4.opPattern","COPY",FACE,{"derivedFrom":subQ0,"instanceName":"38"}),makeQuery(id+"F4.opPattern","COPY",FACE,{"derivedFrom":subQ0,"instanceName":"39"}),makeQuery(id+"F4.opPattern","COPY",FACE,{"derivedFrom":subQ0,"instanceName":"40"}),makeQuery(id+"F4.opPattern","COPY",FACE,{"derivedFrom":subQ0,"instanceName":"41"}),makeQuery(id+"F4.opPattern","COPY",FACE,{"derivedFrom":subQ0,"instanceName":"42"}),makeQuery(id+"F4.opPattern","COPY",FACE,{"derivedFrom":subQ0,"instanceName":"43"}),makeQuery(id+"F4.opPattern","COPY",FACE,{"derivedFrom":subQ0,"instanceName":"44"}),makeQuery(id+"F4.opPattern","COPY",FACE,{"derivedFrom":subQ0,"instanceName":"45"}),makeQuery(id+"F4.opPattern","COPY",FACE,{"derivedFrom":subQ0,"instanceName":"46"}),makeQuery(id+"F4.opPattern","COPY",FACE,{"derivedFrom":subQ0,"instanceName":"47"})]}),makeQuery(id+"F11.opExtrude","SWEPT_FACE",FACE,{"disambiguationData":[OSD([sQuery(id+"F8.wireOp",EDGE,"E22")])]})]});}
            var Q6;
            Q6=makeQuery(id+"F14.boolean.opBoolean","INTERSECT",EDGE,{"disambiguationData":[OD(1.0)],"derivedFrom":[makeQuery(id+"F6.opExtrude","SWEPT_FACE",FACE,{"disambiguationData":[OSD([sQuery(id+"F5.wireOp",EDGE,"E17")])]}),makeQuery(id+"F14.opExtrude","SWEPT_FACE",FACE,{"disambiguationData":[OSD([sQuery(id+"F13.wireOp",EDGE,"E26")])]})]});
            var Q7;
            Q7=makeQuery(id+"F14.boolean.opBoolean","INTERSECT",EDGE,{"disambiguationData":[OD(0.0)],"derivedFrom":[makeQuery(id+"F6.opExtrude","SWEPT_FACE",FACE,{"disambiguationData":[OSD([sQuery(id+"F5.wireOp",EDGE,"E17")])]}),makeQuery(id+"F14.opExtrude","SWEPT_FACE",FACE,{"disambiguationData":[OSD([sQuery(id+"F13.wireOp",EDGE,"E26")])]})]});
            var Q8;
            Q8=makeQuery(id+"F7.boolean.opBoolean","COPY",EDGE,{"derivedFrom":makeQuery(id+"F7.opExtrude","CAP_EDGE",EDGE,{"disambiguationData":[OSD([sQuery(id+"F0.wireOp",EDGE,"E15")])],"isStart":false})});
            var Q9;
            Q9=makeQuery(id+"F7.boolean.opBoolean","COPY",EDGE,{"derivedFrom":makeQuery(id+"F7.opExtrude","CAP_EDGE",EDGE,{"disambiguationData":[OSD([sQuery(id+"F0.wireOp",EDGE,"E16")])],"isStart":false})});
            var Q10;
            Q10=makeQuery(id+"F6.opExtrude","CAP_EDGE",EDGE,{"disambiguationData":[OSD([sQuery(id+"F5.wireOp",EDGE,"E17")])],"isStart":false});
            fillet(context, id + "F15", {"entities" : qUnion([Q0, Q1, Q2, Q3, Q4, Q5, Q6, Q7, Q8, Q9, Q10]), "radius" : 0.5 * mm, "tangentPropagation" : true, "allowEdgeOverflow" : false});
        }
    });
